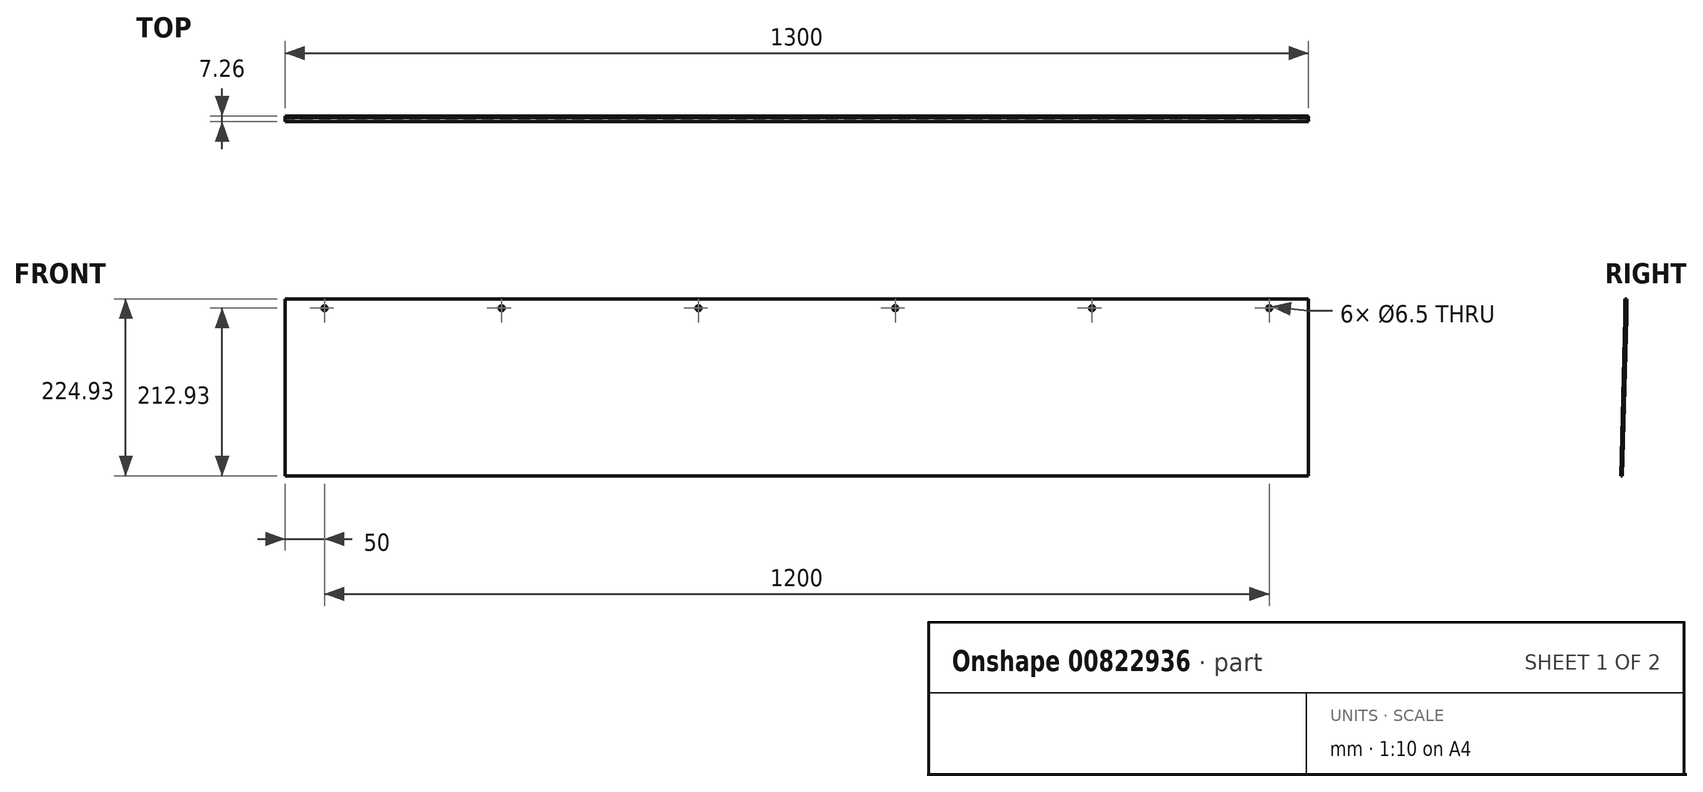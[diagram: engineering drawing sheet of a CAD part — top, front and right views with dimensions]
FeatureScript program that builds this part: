
annotation { "Feature Type Name" : "Feature", "Feature Type Description" : "" }
export const myFeature = defineFeature(function(context is Context, id is Id, definition is map)
    precondition{}
    {
        {
            var Q0;
            Q0=qCreatedBy(makeId("Right.planeOp"),FACE);
            var sketch = newSketch(context, id + "F0", { "sketchPlane" : qUnion([Q0])});
            skLineSegment(sketch, "E0", {"start": v(0, 0) * mm, "end": v(0, -24) * mm});
            skLineSegment(sketch, "E1", {"start": v(0, -24) * mm, "end": v(-5.26, -224.93) * mm});
            skLineSegment(sketch, "E2", {"start": v(-5.26, -224.93) * mm, "end": v(-7.26, -224.88) * mm});
            skLineSegment(sketch, "E3", {"start": v(-7.26, -224.88) * mm, "end": v(-2, -23.97) * mm});
            skLineSegment(sketch, "E4", {"start": v(0, 0) * mm, "end": v(-2, 0) * mm});
            skLineSegment(sketch, "E5", {"start": v(-2, 0) * mm, "end": v(-2, -23.97) * mm});
            skSolve(sketch);
        }
        {
            var Q0;
            Q0 = qSketchRegion(id + "F0", true);
            extrude(context, id + "F1", {"entities" : qUnion([Q0]), "endBound" : BoundingType.SYMMETRIC, "depth" : 1300 * mm, "offsetDistance" : 25 * mm});
        }
        {
            var Q0;
            Q0=makeQuery(id+"F1.opExtrude","SWEPT_FACE",FACE,{"disambiguationData":[OSD([sQuery(id+"F0.wireOp",EDGE,"E0")])]});
            var sketch = newSketch(context, id + "F2", { "sketchPlane" : qUnion([Q0])});
            skLineSegment(sketch, "E6.0.0", {"start": v(650, -24) * mm, "end": v(650, 0) * mm, "construction": true});
            skLineSegment(sketch, "E6.0.1", {"start": v(650, 0) * mm, "end": v(-650, 0) * mm, "construction": true});
            skLineSegment(sketch, "E6.0.2", {"start": v(-650, 0) * mm, "end": v(-650, -24) * mm, "construction": true});
            skLineSegment(sketch, "E6.0.3", {"start": v(-650, -24) * mm, "end": v(650, -24) * mm, "construction": true});
            skLineSegment(sketch, "E7", {"start": v(-650, -12) * mm, "end": v(650, -12) * mm, "construction": true});
            skLineSegment(sketch, "E8", {"start": v(0, 0) * mm, "end": v(0, -24) * mm, "construction": true});
            skLineSegment(sketch, "E9", {"start": v(0, 0) * mm, "end": v(0, 56.44) * mm, "construction": true});
            skCircle(sketch, "E10", {"center": v(-600, -12) * mm, "radius": 3.25 * mm});
            skCircle(sketch, "E11", {"center": v(-375, -12) * mm, "radius": 3.25 * mm});
            skCircle(sketch, "E12", {"center": v(-125, -12) * mm, "radius": 3.25 * mm});
            skCircle(sketch, "E13.MirrorC", {"center": v(600, -12) * mm, "radius": 3.25 * mm});
            skCircle(sketch, "E14.MirrorC", {"center": v(375, -12) * mm, "radius": 3.25 * mm});
            skCircle(sketch, "E15.MirrorC", {"center": v(125, -12) * mm, "radius": 3.25 * mm});
            skSolve(sketch);
        }
        {
            var Q0;
            Q0 = qSketchRegion(id + "F2", true);
            extrude(context, id + "F3", {"entities" : qUnion([Q0]), "operationType" : NewBodyOperationType.REMOVE, "oppositeDirection" : true, "depth" : 25 * mm, "offsetDistance" : 25 * mm});
        }
        {
            var Q0;
            Q0=makeQuery(id+"F1.opExtrude","SWEPT_EDGE",EDGE,{"disambiguationData":[OSD([sQuery(id+"F0.wireOp",EDGE,"E3"),sQuery(id+"F0.wireOp",EDGE,"E5")])]});
            fillet(context, id + "F4", {"entities" : qUnion([Q0]), "radius" : 2 * mm, "tangentPropagation" : true, "allowEdgeOverflow" : false});
        }
        {
            var Q0;
            Q0=makeQuery(id+"F1.opExtrude","SWEPT_EDGE",EDGE,{"disambiguationData":[OSD([sQuery(id+"F0.wireOp",EDGE,"E0"),sQuery(id+"F0.wireOp",EDGE,"E1")])]});
            fillet(context, id + "F5", {"entities" : qUnion([Q0]), "radius" : 4 * mm, "tangentPropagation" : true, "allowEdgeOverflow" : false});
        }
    });
